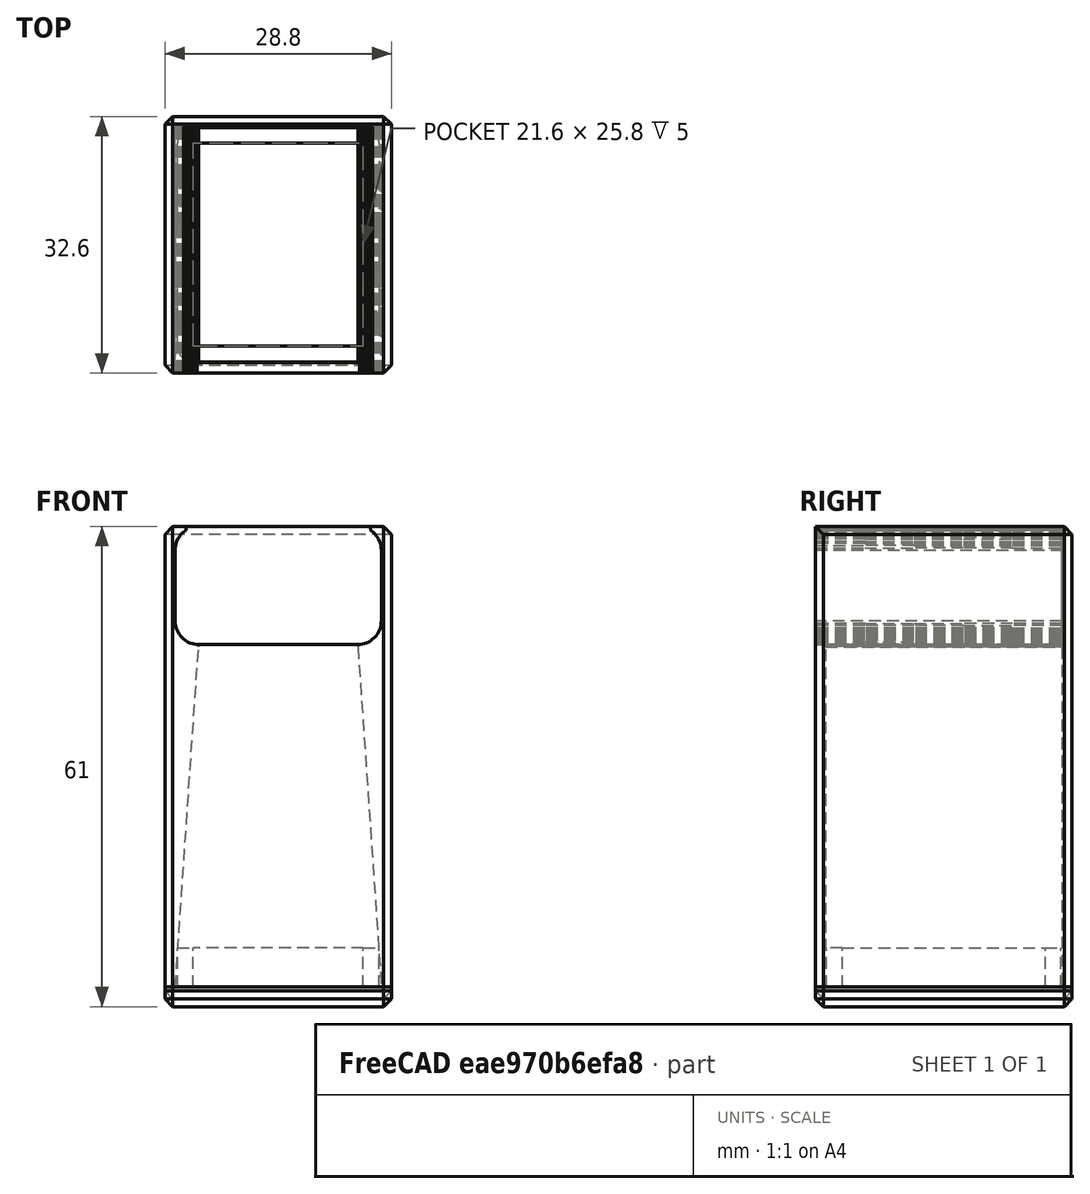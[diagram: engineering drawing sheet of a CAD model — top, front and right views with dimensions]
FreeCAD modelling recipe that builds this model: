
FCSTD DOCUMENT  (FreeCAD 0.20RUnknown)
Label: FilamentCutterBoxBottomFix
License: All rights reserved
LicenseURL: http://en.wikipedia.org/wiki/All_rights_reserved
objects: Part::Feature×2, Sketcher::SketchObject×2, PartDesign::Pad×2, Mesh::Feature×1, PartDesign::SubShapeBinder×1, PartDesign::Fillet×1, PartDesign::Chamfer×1, PartDesign::Body×1
note: 14 computed .brp shape members not serialized (recipe doc carries the construction recipe); baked Part::Feature solids carry a one-line shape summary decoded from their .brp

FEATURE [Mesh::Feature] FilamentCutterBox
FEATURE [Part::Feature] FilamentCutterBox001
  shape: bbox 28.8 x 32.6 x 60 mm, 3272 faces, 0 solids (baked)
FEATURE [Part::Feature] FilamentCutterBox001_solid  label="FilamentCutterBox001 (Solid)"
  shape: bbox 28.8 x 32.6 x 60 mm, 3272 faces (baked)
FEATURE [PartDesign::SubShapeBinder] Binder
  BindCopyOnChange = 0
  BindMode = 0
  ClaimChildren = false
  Context = -> Body [Binder.]
  Fuse = false
  MakeFace = true
  OffsetFill = false
  OffsetIntersection = false
  OffsetJoinType = 0
  OffsetOpenResult = false
  PartialLoad = false
  Relative = true
  Support = -> [FilamentCutterBox001_solid]
  _Version = 2
FEATURE [Sketcher::SketchObject] Sketch
  ExternalGeometry = -> [Binder]
  FullyConstrained = true
  MapMode = 5
  Placement = pos=(0,0,1.5) rot=(0,0,1;0rad)
  Support = -> [Binder]
  sketch-geometry (12):
    g0: LineSegment StartX=-1.3 StartY=30.3 StartZ=0 EndX=-1.3 EndY=31.3 EndZ=0
    g1: LineSegment StartX=-1.3 StartY=31.3 StartZ=0 EndX=-0.3 EndY=31.3 EndZ=0
    g2: LineSegment StartX=26.5 StartY=31.3 StartZ=0 EndX=27.5 EndY=31.3 EndZ=0
    g3: LineSegment StartX=27.5 StartY=31.3 StartZ=0 EndX=27.5 EndY=30.3 EndZ=0
    g4: LineSegment StartX=27.5 StartY=-0.3 StartZ=0 EndX=27.5 EndY=-1.3 EndZ=0
    g5: LineSegment StartX=27.5 StartY=-1.3 StartZ=0 EndX=23.4249 EndY=-1.3 EndZ=0
    g6: LineSegment StartX=-1.3 StartY=-0.3 StartZ=0 EndX=-1.3 EndY=-1.3 EndZ=0
    g7: LineSegment StartX=-1.3 StartY=-1.3 StartZ=0 EndX=2.7751 EndY=-1.3 EndZ=0
    g8: LineSegment StartX=-1.3 StartY=-1.3 StartZ=0 EndX=27.5 EndY=-1.3 EndZ=0
    g9: LineSegment StartX=27.5 StartY=-1.3 StartZ=0 EndX=27.5 EndY=31.3 EndZ=0
    g10: LineSegment StartX=27.5 StartY=31.3 StartZ=0 EndX=-1.3 EndY=31.3 EndZ=0
    g11: LineSegment StartX=-1.3 StartY=31.3 StartZ=0 EndX=-1.3 EndY=-1.3 EndZ=0
  constraints (30):
    c: Coincident(g-5,g0)
    c: Vertical(g0)
    c: Coincident(g0,g1)
    c: Coincident(g1,g-3)
    c: Horizontal(g1)
    c: Coincident(g-3,g2)
    c: Horizontal(g2)
    c: Coincident(g2,g3)
    c: Coincident(g3,g-4)
    c: Vertical(g3)
    c: Coincident(g-4,g4)
    c: Vertical(g4)
    c: Coincident(g4,g5)
    c: Coincident(g5,g-6)
    c: Coincident(g-5,g6)
    c: Vertical(g6)
    c: Coincident(g6,g7)
    c: Coincident(g7,g-6)
    c: Horizontal(g5)
    c: Horizontal(g7)
    c: Coincident(g8,g9)
    c: Coincident(g9,g10)
    c: Coincident(g10,g11)
    c: Coincident(g11,g8)
    c: Horizontal(g8)
    c: Horizontal(g10)
    c: Vertical(g9)
    c: Vertical(g11)
    c: Coincident(g8,g6)
    c: Coincident(g9,g2)
FEATURE [PartDesign::Pad] Pad
  Direction = (0,0,1)
  Length = 2.5
  Length2 = 10
  Profile = -> Sketch
  ReferenceAxis = -> Sketch [N_Axis]
  Reversed = true
  Type = 0
FEATURE [Sketcher::SketchObject] Sketch001
  ExternalGeometry = -> [Binder]
  FullyConstrained = true
  MapMode = 5
  Placement = pos=(0,0,1.5) rot=(0,0,1;0rad)
  Support = -> [Binder]
  sketch-geometry (8):
    g0: LineSegment StartX=0.3 StartY=29.9 StartZ=0 EndX=25.9 EndY=29.9 EndZ=0
    g1: LineSegment StartX=25.9 StartY=29.9 StartZ=0 EndX=25.9 EndY=0.1 EndZ=0
    g2: LineSegment StartX=25.9 StartY=0.1 StartZ=0 EndX=0.3 EndY=0.1 EndZ=0
    g3: LineSegment StartX=0.3 StartY=0.1 StartZ=0 EndX=0.3 EndY=29.9 EndZ=0
    g4: LineSegment StartX=23.9 StartY=27.9 StartZ=0 EndX=2.3 EndY=27.9 EndZ=0
    g5: LineSegment StartX=2.3 StartY=27.9 StartZ=0 EndX=2.3 EndY=2.1 EndZ=0
    g6: LineSegment StartX=2.3 StartY=2.1 StartZ=0 EndX=23.9 EndY=2.1 EndZ=0
    g7: LineSegment StartX=23.9 StartY=2.1 StartZ=0 EndX=23.9 EndY=27.9 EndZ=0
  constraints (24):
    c: Coincident(g0,g1)
    c: Coincident(g1,g2)
    c: Coincident(g2,g3)
    c: Coincident(g3,g0)
    c: Horizontal(g0)
    c: Horizontal(g2)
    c: Vertical(g1)
    c: Vertical(g3)
    c: Coincident(g4,g5)
    c: Coincident(g5,g6)
    c: Coincident(g6,g7)
    c: Coincident(g7,g4)
    c: Horizontal(g4)
    c: Horizontal(g6)
    c: Vertical(g5)
    c: Vertical(g7)
    c: DistanceY(g4,g0) = 2
    c: DistanceX(g4,g0) = 2
    c: DistanceX(g2,g5) = 2
    c: DistanceY(g2,g5) = 2
    c: DistanceY(g0,g-6) = 1.4
    c: DistanceX(g-7,g0) = 1.6
    c: DistanceY(g-8,g1) = 1.4
    c: DistanceX(g1,g-5) = 1.6
FEATURE [PartDesign::Pad] Pad001
  BaseFeature = -> Pad
  Direction = (0,0,1)
  Length = 5
  Length2 = 10
  Profile = -> Sketch001
  ReferenceAxis = -> Sketch001 [N_Axis]
  Type = 0
FEATURE [PartDesign::Fillet] Fillet
  Base = -> Pad001 [Edge22,Edge18,Edge20,Edge17]
  BaseFeature = -> Pad001
  Radius = 2
  SupportTransform = false
  UseAllEdges = false
FEATURE [PartDesign::Chamfer] Chamfer
  Angle = 45
  Base = -> Fillet [Face15,Edge29,Edge30,Edge32,Edge34]
  BaseFeature = -> Fillet
  ChamferType = 0
  FlipDirection = false
  Size = 1
  Size2 = 1
  SupportTransform = false
  UseAllEdges = false
FEATURE [PartDesign::Body] Body
  Group = -> [Binder,Sketch,Pad,Sketch001,Pad001,Fillet,Chamfer]
  Origin = -> Origin
  Tip = -> Chamfer
